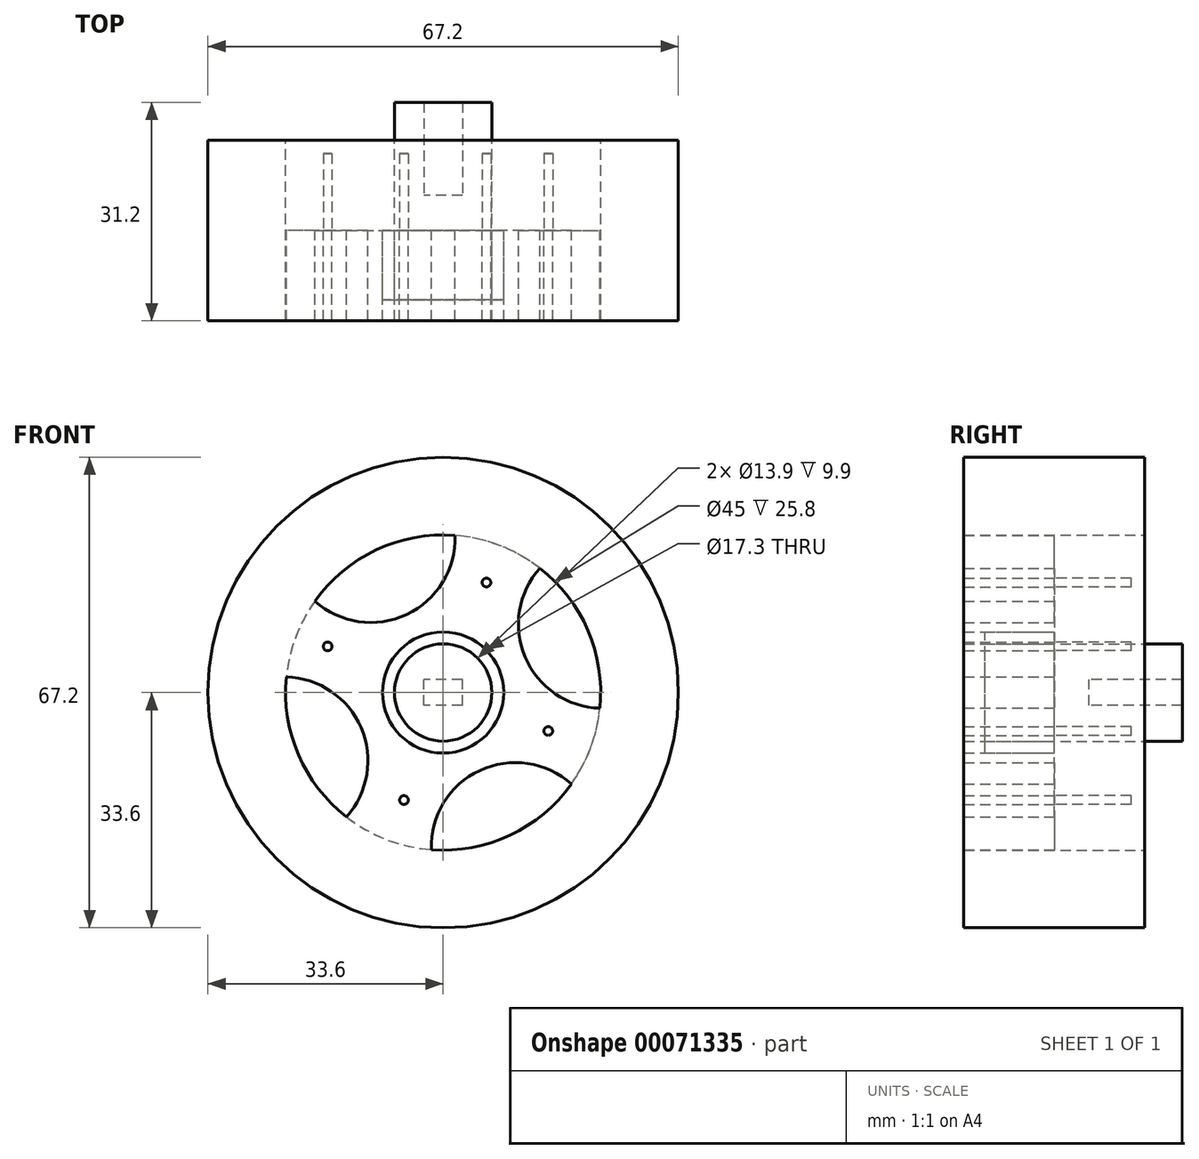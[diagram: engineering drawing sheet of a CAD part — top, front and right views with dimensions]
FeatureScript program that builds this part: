
annotation { "Feature Type Name" : "Feature", "Feature Type Description" : "" }
export const myFeature = defineFeature(function(context is Context, id is Id, definition is map)
    precondition{}
    {
        {
            var Q0;
            Q0=qCreatedBy(makeId("Front.planeOp"),FACE);
            var sketch = newSketch(context, id + "F0", { "sketchPlane" : qUnion([Q0])});
            skCircle(sketch, "E0", {"center": v(0, 0) * mm, "radius": 22.5 * mm});
            skCircle(sketch, "E1", {"center": v(0, 0) * mm, "radius": 6.95 * mm});
            skCircle(sketch, "E2", {"center": v(0, 0) * mm, "radius": 8.65 * mm});
            skLineSegment(sketch, "E3.bottom", {"start": v(2.75, -1.85) * mm, "end": v(-2.75, -1.85) * mm});
            skLineSegment(sketch, "E3.top", {"start": v(2.75, 1.85) * mm, "end": v(-2.75, 1.85) * mm});
            skLineSegment(sketch, "E3.left", {"start": v(2.75, -1.85) * mm, "end": v(2.75, 1.85) * mm});
            skLineSegment(sketch, "E3.right", {"start": v(-2.75, -1.85) * mm, "end": v(-2.75, 1.85) * mm});
            skArc(sketch, "E4", {"start": v(18.32, -13.06) * mm, "mid": v(5.22, -11.13) * mm, "end": v(-1.68, -22.44) * mm});
            skArc(sketch, "E5", {"start": v(13.81, 17.76) * mm, "mid": v(11.72, 5.03) * mm, "end": v(22.39, -2.24) * mm});
            skArc(sketch, "E6", {"start": v(-18.32, 13.06) * mm, "mid": v(-5.22, 11.13) * mm, "end": v(1.68, 22.44) * mm});
            skArc(sketch, "E7", {"start": v(-13.81, -17.76) * mm, "mid": v(-11.72, -5.03) * mm, "end": v(-22.39, 2.24) * mm});
            skCircle(sketch, "E8", {"center": v(0, 0) * mm, "radius": 24 * mm});
            skCircle(sketch, "E9", {"center": v(15.02, -5.5) * mm, "radius": 0.62 * mm});
            skCircle(sketch, "E10", {"center": v(6.18, 15.71) * mm, "radius": 0.62 * mm});
            skCircle(sketch, "E11", {"center": v(-16.5, 6.58) * mm, "radius": 0.62 * mm});
            skCircle(sketch, "E12", {"center": v(-5.6, -15.36) * mm, "radius": 0.62 * mm});
            skSolve(sketch);
        }
        {
            var Q0;
            Q0=makeQuery(id+"F0.imprint","IMPRINT",FACE,{"disambiguationData":[TD([[makeQuery(id+"F0.imprint","IMPRINT",EDGE,{"derivedFrom":sQuery(id+"F0.wireOp",EDGE,"udhCGNyq-Bzgs-kjSm-Ki08-aSFPeaWiobY3")}),1.0]])]});
            var Q1;
            Q1=makeQuery(id+"F0.imprint","IMPRINT",FACE,{"disambiguationData":[TD([[makeQuery(id+"F0.imprint","IMPRINT",EDGE,{"derivedFrom":sQuery(id+"F0.wireOp",EDGE,"E2")}),-1.0]])]});
            var Q2;
            Q2=makeQuery(id+"F0.imprint","IMPRINT",FACE,{"disambiguationData":[TD([[makeQuery(id+"F0.imprint","IMPRINT",EDGE,{"derivedFrom":sQuery(id+"F0.wireOp",EDGE,"E8")}),1.0]])]});
            extrude(context, id + "F1", {"entities" : qUnion([Q0, Q1, Q2]), "depth" : 12.9 * mm});
        }
        {
            var Q0;
            Q0=makeQuery(id+"F0.imprint","IMPRINT",FACE,{"disambiguationData":[TD([[makeQuery(id+"F0.imprint","IMPRINT",EDGE,{"derivedFrom":sQuery(id+"F0.wireOp",EDGE,"E8")}),1.0]])]});
            extrude(context, id + "F2", {"entities" : qUnion([Q0]), "operationType" : NewBodyOperationType.ADD, "oppositeDirection" : true, "depth" : (12.9) * mm});
        }
        {
            var Q0;
            Q0=makeQuery(id+"F0.imprint","IMPRINT",FACE,{"disambiguationData":[TD([[makeQuery(id+"F0.imprint","IMPRINT",EDGE,{"derivedFrom":sQuery(id+"F0.wireOp",EDGE,"E1")}),1.0]])]});
            var Q1;
            Q1=makeQuery(id+"F0.imprint","IMPRINT",FACE,{"disambiguationData":[TD([[makeQuery(id+"F0.imprint","IMPRINT",EDGE,{"derivedFrom":sQuery(id+"F0.wireOp",EDGE,"E3.bottom")}),-1.0]])]});
            extrude(context, id + "F3", {"entities" : qUnion([Q0, Q1]), "depth" : 12.9 * mm});
        }
        {
            var Q0;
            Q0=makeQuery(id+"F0.imprint","IMPRINT",FACE,{"disambiguationData":[TD([[makeQuery(id+"F0.imprint","IMPRINT",EDGE,{"derivedFrom":sQuery(id+"F0.wireOp",EDGE,"E1")}),-1.0]])]});
            extrude(context, id + "F4", {"entities" : qUnion([Q0]), "depth" : 9.9 * mm});
        }
        {
            var Q0;
            Q0=makeQuery(id+"F0.imprint","IMPRINT",FACE,{"disambiguationData":[TD([[makeQuery(id+"F0.imprint","IMPRINT",EDGE,{"derivedFrom":sQuery(id+"F0.wireOp",EDGE,"E1")}),-1.0]])]});
            extrude(context, id + "F5", {"entities" : qUnion([Q0]), "depth" : 9.9 * mm});
        }
        {
            var Q0;
            Q0=makeQuery(id+"F0.imprint","IMPRINT",FACE,{"disambiguationData":[TD([[makeQuery(id+"F0.imprint","IMPRINT",EDGE,{"derivedFrom":sQuery(id+"F0.wireOp",EDGE,"E1")}),1.0]])]});
            extrude(context, id + "F6", {"entities" : qUnion([Q0]), "oppositeDirection" : true, "depth" : 18.3 * mm});
        }
        {
            var Q0;
            Q0=makeQuery(id+"F0.imprint","IMPRINT",FACE,{"disambiguationData":[TD([[makeQuery(id+"F0.imprint","IMPRINT",EDGE,{"derivedFrom":sQuery(id+"F0.wireOp",EDGE,"E3.bottom")}),-1.0]])]});
            extrude(context, id + "F7", {"entities" : qUnion([Q0]), "operationType" : NewBodyOperationType.ADD, "oppositeDirection" : true, "depth" : 5 * mm});
        }
        {
            var Q0;
            Q0=qCreatedBy(makeId("Front.planeOp"),FACE);
            var sketch = newSketch(context, id + "F8", { "sketchPlane" : qUnion([Q0])});
            skCircle(sketch, "E13", {"center": v(0, 0) * mm, "radius": 33.6 * mm});
            skCircle(sketch, "E14", {"center": v(0, 0) * mm, "radius": 24 * mm});
            skSolve(sketch);
        }
        {
            var Q0;
            Q0=makeQuery(id+"F8.imprint","IMPRINT",FACE,{"disambiguationData":[TD([[makeQuery(id+"F8.imprint","IMPRINT",EDGE,{"derivedFrom":sQuery(id+"F8.wireOp",EDGE,"E13")}),1.0]])]});
            extrude(context, id + "F9", {"entities" : qUnion([Q0]), "depth" : 12.9 * mm});
        }
        {
            var Q0;
            Q0=makeQuery(id+"F9.opExtrude","CAP_FACE",FACE,{"disambiguationData":[OSD([sQuery(id+"F8.wireOp",EDGE,"E13"),sQuery(id+"F8.wireOp",EDGE,"E14")])],"isStart":true});
            extrude(context, id + "F10", {"entities" : qUnion([Q0]), "operationType" : NewBodyOperationType.ADD, "depth" : 12.9 * mm});
        }
        {
            var Q0;
            Q0=makeQuery(id+"F0.imprint","IMPRINT",FACE,{"disambiguationData":[TD([[makeQuery(id+"F0.imprint","IMPRINT",EDGE,{"derivedFrom":sQuery(id+"F0.wireOp",EDGE,"E10")}),1.0]])]});
            var Q1;
            Q1=makeQuery(id+"F0.imprint","IMPRINT",FACE,{"disambiguationData":[TD([[makeQuery(id+"F0.imprint","IMPRINT",EDGE,{"derivedFrom":sQuery(id+"F0.wireOp",EDGE,"E11")}),1.0]])]});
            var Q2;
            Q2=makeQuery(id+"F0.imprint","IMPRINT",FACE,{"disambiguationData":[TD([[makeQuery(id+"F0.imprint","IMPRINT",EDGE,{"derivedFrom":sQuery(id+"F0.wireOp",EDGE,"E9")}),1.0]])]});
            var Q3;
            Q3=makeQuery(id+"F0.imprint","IMPRINT",FACE,{"disambiguationData":[TD([[makeQuery(id+"F0.imprint","IMPRINT",EDGE,{"derivedFrom":sQuery(id+"F0.wireOp",EDGE,"E12")}),1.0]])]});
            extrude(context, id + "F11", {"entities" : qUnion([Q0, Q1, Q2, Q3]), "operationType" : NewBodyOperationType.ADD, "oppositeDirection" : true, "depth" : 11 * mm});
        }
    });
